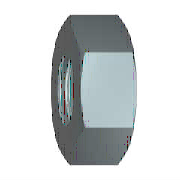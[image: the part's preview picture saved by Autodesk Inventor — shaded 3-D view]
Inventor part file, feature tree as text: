
AUTODESK INVENTOR PART (.ipt)
format: ipt  version: 2022 (Build 260153000, 153)  size: 173,568 bytes
history: native  units: mm (DEFAULTED — no unit token found)
features: sketch x3, other x2, extrude x1, hole x1, plane x1
ambient origin geometry x7: Origin, YZ Plane, XZ Plane, X Axis, Y Axis, Z Axis, Center Point
bodies: Solid1 (feature_tree)
feature tree (8):
  extrude  "Базовый элемент"  Depth=6.350853mm
  other  "Фаска1"
  hole  "Резьба"  [1 undecoded]
  other  "Work Axis1"
  plane  "Work Plane1"
  sketch  "Эскиз1"
  sketch  "Эскиз2"
  sketch  "Эскиз3"
note: 1 required parameter value undecoded (feature->parameter linkage not recoverable at this tier; creation-order binding heuristic only, values carry confidence <= 0.55)
